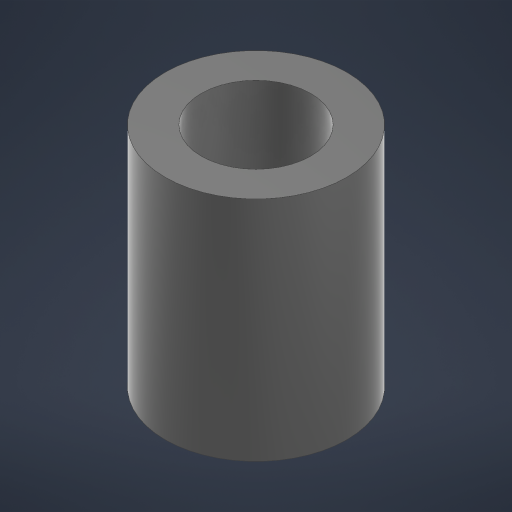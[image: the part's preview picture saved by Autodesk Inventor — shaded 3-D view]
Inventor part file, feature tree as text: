
AUTODESK INVENTOR PART (.ipt)
format: ipt  version: 2024.2 (Build 282272000, 272)  size: 177,152 bytes
history: native  units: mm
features: extrude x1, sketch x1, other x1
ambient origin geometry x8: Origin, YZ Plane, XZ Plane, XY Plane, X Axis, Y Axis, Z Axis, Center Point
bodies: Solid1 (feature_tree)
feature tree (3):
  extrude  "Extrusion1"  Depth=5.0mm
  sketch  "Sketch1"  dims[d0=2.4mm d1=4.0mm d2=5.0mm d3=0.0mm]
  other  "Finish1"
